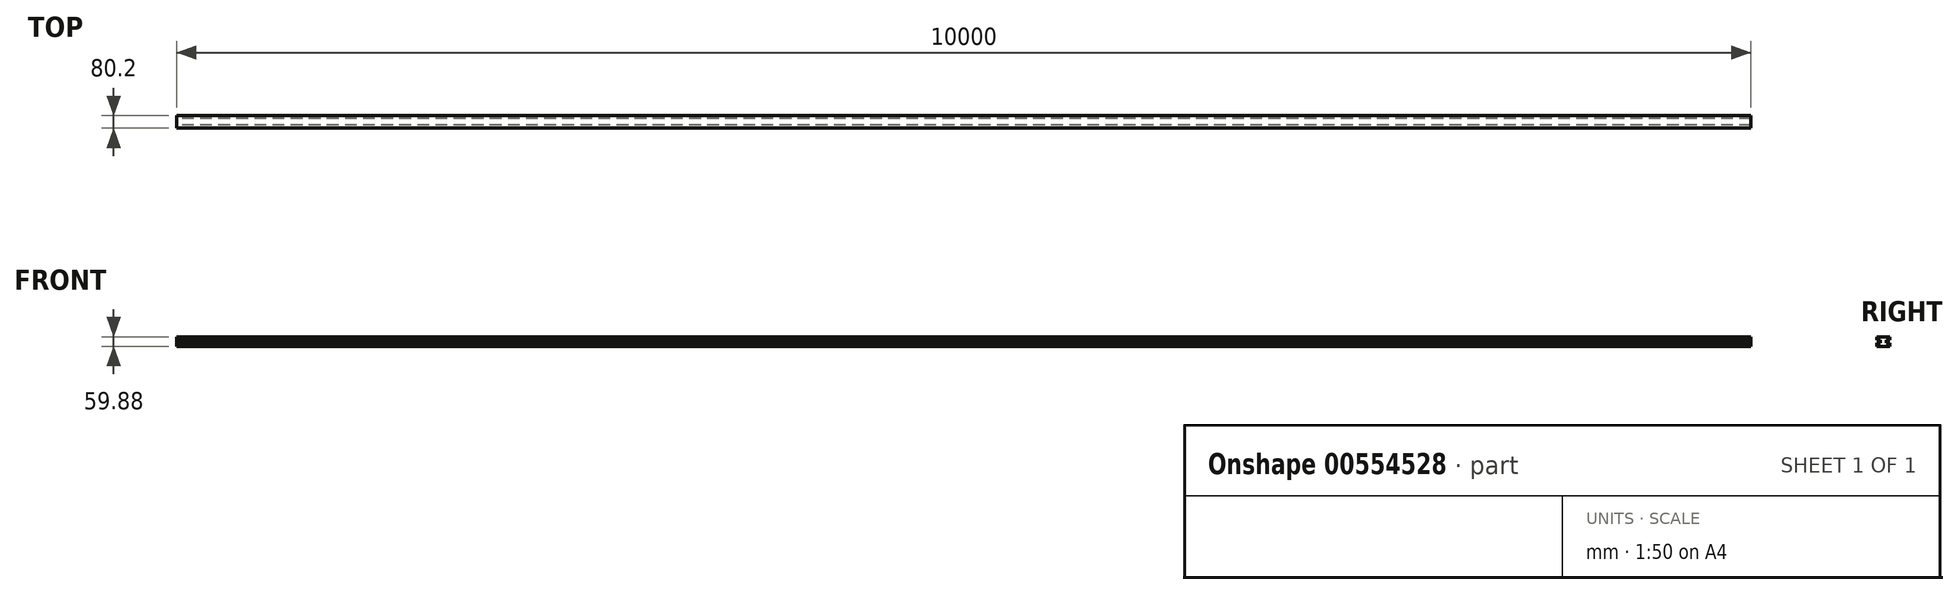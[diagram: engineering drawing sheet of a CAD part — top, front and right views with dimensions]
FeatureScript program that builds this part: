
annotation { "Feature Type Name" : "Feature", "Feature Type Description" : "" }
export const myFeature = defineFeature(function(context is Context, id is Id, definition is map)
    precondition{}
    {
        {
            var Q0;
            Q0=qCreatedBy(makeId("Right.planeOp"),FACE);
            var sketch = newSketch(context, id + "F0", { "sketchPlane" : qUnion([Q0])});
            skLineSegment(sketch, "E0", {"start": v(0, 0) * mm, "end": v(80.2, 0) * mm});
            skLineSegment(sketch, "E1", {"start": v(80.2, 0) * mm, "end": v(80.2, 19.6) * mm});
            skLineSegment(sketch, "E2", {"start": v(80.2, 19.6) * mm, "end": v(60.6, 19.6) * mm});
            skLineSegment(sketch, "E3", {"start": v(60.6, 19.6) * mm, "end": v(60.6, 39.92) * mm});
            skLineSegment(sketch, "E4", {"start": v(60.6, 39.92) * mm, "end": v(80.2, 39.92) * mm});
            skLineSegment(sketch, "E5", {"start": v(80.2, 39.92) * mm, "end": v(80.2, 59.88) * mm});
            skLineSegment(sketch, "E6", {"start": v(80.2, 59.88) * mm, "end": v(0, 59.88) * mm});
            skLineSegment(sketch, "E7", {"start": v(0, 59.88) * mm, "end": v(0, 39.92) * mm});
            skLineSegment(sketch, "E8", {"start": v(0, 39.92) * mm, "end": v(20.32, 39.92) * mm});
            skLineSegment(sketch, "E9", {"start": v(20.32, 39.92) * mm, "end": v(20.32, 19.6) * mm});
            skLineSegment(sketch, "E10", {"start": v(20.32, 19.6) * mm, "end": v(0, 19.6) * mm});
            skLineSegment(sketch, "E11", {"start": v(0, 19.6) * mm, "end": v(0, 0) * mm});
            skSolve(sketch);
        }
        {
            var Q0;
            Q0=makeQuery(id+"F0.imprint","IMPRINT",FACE,{"disambiguationData":[TD([[makeQuery(id+"F0.imprint","IMPRINT",EDGE,{"derivedFrom":sQuery(id+"F0.wireOp",EDGE,"E0")}),1.0]])]});
            extrude(context, id + "F1", {"entities" : qUnion([Q0]), "depth" : 10000 * mm, "offsetDistance" : 25 * mm});
        }
    });
